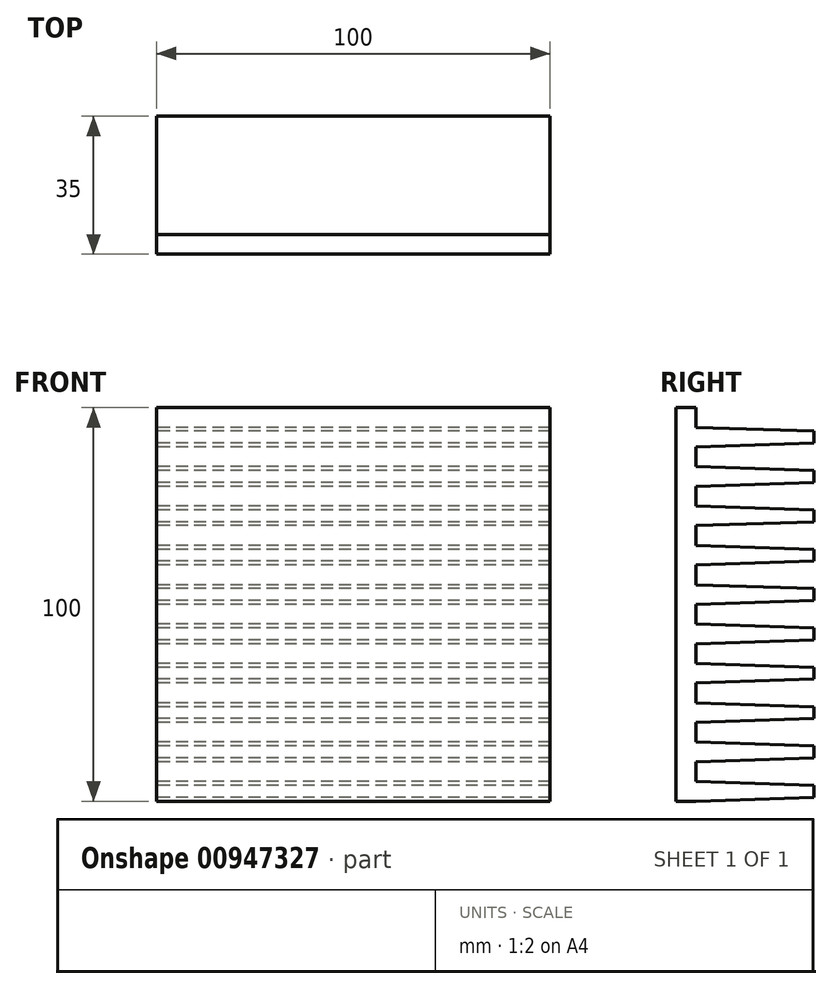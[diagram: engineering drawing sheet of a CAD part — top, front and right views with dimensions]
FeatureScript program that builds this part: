
annotation { "Feature Type Name" : "Feature", "Feature Type Description" : "" }
export const myFeature = defineFeature(function(context is Context, id is Id, definition is map)
    precondition{}
    {
        {
            var Q0;
            Q0=qCreatedBy(makeId("Front.planeOp"),FACE);
            var sketch = newSketch(context, id + "F0", { "sketchPlane" : qUnion([Q0])});
            skLineSegment(sketch, "E0", {"start": v(5, 0) * mm, "end": v(35, 1) * mm});
            skLineSegment(sketch, "E1", {"start": v(35, 1) * mm, "end": v(35, 4) * mm});
            skLineSegment(sketch, "E2", {"start": v(35, 4) * mm, "end": v(5, 5) * mm});
            skLineSegment(sketch, "E3", {"start": v(5, 5) * mm, "end": v(5, 10) * mm});
            skLineSegment(sketch, "E4.0.1.0", {"start": v(5, 15) * mm, "end": v(5, 20) * mm});
            skLineSegment(sketch, "E4.0.1.1", {"start": v(35, 14) * mm, "end": v(5, 15) * mm});
            skLineSegment(sketch, "E4.0.1.2", {"start": v(5, 10) * mm, "end": v(35, 11) * mm});
            skLineSegment(sketch, "E4.0.1.3", {"start": v(35, 11) * mm, "end": v(35, 14) * mm});
            skLineSegment(sketch, "E4.0.2.0", {"start": v(5, 25) * mm, "end": v(5, 30) * mm});
            skLineSegment(sketch, "E4.0.2.1", {"start": v(35, 24) * mm, "end": v(5, 25) * mm});
            skLineSegment(sketch, "E4.0.2.2", {"start": v(5, 20) * mm, "end": v(35, 21) * mm});
            skLineSegment(sketch, "E4.0.2.3", {"start": v(35, 21) * mm, "end": v(35, 24) * mm});
            skLineSegment(sketch, "E4.0.3.0", {"start": v(5, 35) * mm, "end": v(5, 40) * mm});
            skLineSegment(sketch, "E4.0.3.1", {"start": v(35, 34) * mm, "end": v(5, 35) * mm});
            skLineSegment(sketch, "E4.0.3.2", {"start": v(5, 30) * mm, "end": v(35, 31) * mm});
            skLineSegment(sketch, "E4.0.3.3", {"start": v(35, 31) * mm, "end": v(35, 34) * mm});
            skLineSegment(sketch, "E4.0.4.0", {"start": v(5, 45) * mm, "end": v(5, 50) * mm});
            skLineSegment(sketch, "E4.0.4.1", {"start": v(35, 44) * mm, "end": v(5, 45) * mm});
            skLineSegment(sketch, "E4.0.4.2", {"start": v(5, 40) * mm, "end": v(35, 41) * mm});
            skLineSegment(sketch, "E4.0.4.3", {"start": v(35, 41) * mm, "end": v(35, 44) * mm});
            skLineSegment(sketch, "E4.0.5.0", {"start": v(5, 55) * mm, "end": v(5, 60) * mm});
            skLineSegment(sketch, "E4.0.5.1", {"start": v(35, 54) * mm, "end": v(5, 55) * mm});
            skLineSegment(sketch, "E4.0.5.2", {"start": v(5, 50) * mm, "end": v(35, 51) * mm});
            skLineSegment(sketch, "E4.0.5.3", {"start": v(35, 51) * mm, "end": v(35, 54) * mm});
            skLineSegment(sketch, "E4.0.6.0", {"start": v(5, 65) * mm, "end": v(5, 70) * mm});
            skLineSegment(sketch, "E4.0.6.1", {"start": v(35, 64) * mm, "end": v(5, 65) * mm});
            skLineSegment(sketch, "E4.0.6.2", {"start": v(5, 60) * mm, "end": v(35, 61) * mm});
            skLineSegment(sketch, "E4.0.6.3", {"start": v(35, 61) * mm, "end": v(35, 64) * mm});
            skLineSegment(sketch, "E4.0.7.0", {"start": v(5, 75) * mm, "end": v(5, 80) * mm});
            skLineSegment(sketch, "E4.0.7.1", {"start": v(35, 74) * mm, "end": v(5, 75) * mm});
            skLineSegment(sketch, "E4.0.7.2", {"start": v(5, 70) * mm, "end": v(35, 71) * mm});
            skLineSegment(sketch, "E4.0.7.3", {"start": v(35, 71) * mm, "end": v(35, 74) * mm});
            skLineSegment(sketch, "E4.0.8.0", {"start": v(5, 85) * mm, "end": v(5, 90) * mm});
            skLineSegment(sketch, "E4.0.8.1", {"start": v(35, 84) * mm, "end": v(5, 85) * mm});
            skLineSegment(sketch, "E4.0.8.2", {"start": v(5, 80) * mm, "end": v(35, 81) * mm});
            skLineSegment(sketch, "E4.0.8.3", {"start": v(35, 81) * mm, "end": v(35, 84) * mm});
            skLineSegment(sketch, "E4.0.9.0", {"start": v(5, 95) * mm, "end": v(5, 100) * mm});
            skLineSegment(sketch, "E4.0.9.1", {"start": v(35, 94) * mm, "end": v(5, 95) * mm});
            skLineSegment(sketch, "E4.0.9.2", {"start": v(5, 90) * mm, "end": v(35, 91) * mm});
            skLineSegment(sketch, "E4.0.9.3", {"start": v(35, 91) * mm, "end": v(35, 94) * mm});
            skLineSegment(sketch, "E4.direction1", {"start": v(5, 0) * mm, "end": v(30, 0) * mm, "construction": true});
            skLineSegment(sketch, "E4.direction2", {"start": v(5, 0) * mm, "end": v(5, 10) * mm, "construction": true});
            skLineSegment(sketch, "E5", {"start": v(5, 0) * mm, "end": v(0, 0) * mm});
            skLineSegment(sketch, "E6", {"start": v(0, 0) * mm, "end": v(0, 100) * mm});
            skLineSegment(sketch, "E7", {"start": v(0, 100) * mm, "end": v(5, 100) * mm});
            skSolve(sketch);
        }
        {
            var Q0;
            Q0=makeQuery(id+"F0.imprint","IMPRINT",FACE,{"disambiguationData":[TD([[makeQuery(id+"F0.imprint","IMPRINT",EDGE,{"derivedFrom":sQuery(id+"F0.wireOp",EDGE,"E0")}),1.0]])]});
            extrude(context, id + "F1", {"entities" : qUnion([Q0]), "depth" : 100 * mm, "offsetDistance" : 25 * mm});
        }
        {
            var Q0;
            Q0=makeQuery(id+"F1.opExtrude","SWEPT_BODY",BODY,{"disambiguationData":[OSD([sQuery(id+"F0.wireOp",EDGE,"E0"),sQuery(id+"F0.wireOp",EDGE,"E1"),sQuery(id+"F0.wireOp",EDGE,"E2"),sQuery(id+"F0.wireOp",EDGE,"E3"),sQuery(id+"F0.wireOp",EDGE,"E4.0.1.0"),sQuery(id+"F0.wireOp",EDGE,"E4.0.1.1"),sQuery(id+"F0.wireOp",EDGE,"E4.0.1.2"),sQuery(id+"F0.wireOp",EDGE,"E4.0.1.3"),sQuery(id+"F0.wireOp",EDGE,"E4.0.2.0"),sQuery(id+"F0.wireOp",EDGE,"E4.0.2.1"),sQuery(id+"F0.wireOp",EDGE,"E4.0.2.2"),sQuery(id+"F0.wireOp",EDGE,"E4.0.2.3"),sQuery(id+"F0.wireOp",EDGE,"E4.0.3.0"),sQuery(id+"F0.wireOp",EDGE,"E4.0.3.1"),sQuery(id+"F0.wireOp",EDGE,"E4.0.3.2"),sQuery(id+"F0.wireOp",EDGE,"E4.0.3.3"),sQuery(id+"F0.wireOp",EDGE,"E4.0.4.0"),sQuery(id+"F0.wireOp",EDGE,"E4.0.4.1"),sQuery(id+"F0.wireOp",EDGE,"E4.0.4.2"),sQuery(id+"F0.wireOp",EDGE,"E4.0.4.3"),sQuery(id+"F0.wireOp",EDGE,"E4.0.5.0"),sQuery(id+"F0.wireOp",EDGE,"E4.0.5.1"),sQuery(id+"F0.wireOp",EDGE,"E4.0.5.2"),sQuery(id+"F0.wireOp",EDGE,"E4.0.5.3"),sQuery(id+"F0.wireOp",EDGE,"E4.0.6.0"),sQuery(id+"F0.wireOp",EDGE,"E4.0.6.1"),sQuery(id+"F0.wireOp",EDGE,"E4.0.6.2"),sQuery(id+"F0.wireOp",EDGE,"E4.0.6.3"),sQuery(id+"F0.wireOp",EDGE,"E4.0.7.0"),sQuery(id+"F0.wireOp",EDGE,"E4.0.7.1"),sQuery(id+"F0.wireOp",EDGE,"E4.0.7.2"),sQuery(id+"F0.wireOp",EDGE,"E4.0.7.3"),sQuery(id+"F0.wireOp",EDGE,"E4.0.8.0"),sQuery(id+"F0.wireOp",EDGE,"E4.0.8.1"),sQuery(id+"F0.wireOp",EDGE,"E4.0.8.2"),sQuery(id+"F0.wireOp",EDGE,"E4.0.8.3"),sQuery(id+"F0.wireOp",EDGE,"E4.0.9.0"),sQuery(id+"F0.wireOp",EDGE,"E4.0.9.1"),sQuery(id+"F0.wireOp",EDGE,"E4.0.9.2"),sQuery(id+"F0.wireOp",EDGE,"E4.0.9.3"),sQuery(id+"F0.wireOp",EDGE,"E5"),sQuery(id+"F0.wireOp",EDGE,"E6"),sQuery(id+"F0.wireOp",EDGE,"E7")])]});
            var Q1;
            Q1=makeQuery(id+"F1.opExtrude","CAP_EDGE",EDGE,{"disambiguationData":[OSD([sQuery(id+"F0.wireOp",EDGE,"E6")])],"isStart":true});
            transform(context, id + "F2", {"entities" : qUnion([Q0]), "transformType" : TransformType.ROTATION, "transformAxis" : qUnion([Q1]), "angle" : 90 * degree, "makeCopy" : false});
        }
    });
